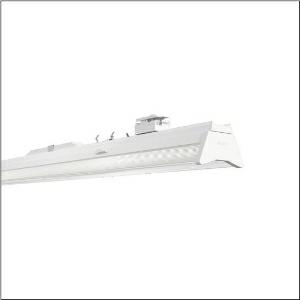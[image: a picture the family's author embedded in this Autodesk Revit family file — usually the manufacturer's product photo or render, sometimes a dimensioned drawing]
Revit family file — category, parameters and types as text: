
# Revit family: licross_r__21_performance_mo_51td16vn48xg_f21d
name_source: partatom
category: Lighting Fixtures
units: mm (PartAtom-declared; Revit-internal decimal feet)

## family parameters
Cut with Voids When Loaded = No
Host = Face
Light Source = No
Part Type = Normal
Room Calculation Point = No
Round Connector Dimension = Use Diameter
Shared = No

## types (1)
- --- (1 x LED, 8000 lm, 44.1 W, 4000K)
    Apparent Load = 44 VA
    CIE Flux Codes = 66 88 96 79 100
    Color Rendering = 80
    Color Temperature = 4000K
    Default Elevation = 1800 mm
    Description = Licross® 21 Performance MO, luminaire insert, of sheet steel, galvanised, coil coated, white, length: 1.500mm, width: 120mm, height: 123mm, LED rated luminous flux: 8.000lm, light colour: 840, control gear: DALI 2, CLO, with plug, 5-pole, with phase selection, mains connection: 220..240V, AC, 50/60Hz, start of lifetime: 44W, end of service life: 49W, internal wiring halogen-free, primary light control with lens, of plastic, primary optical cover: cover, of PMMA, light emission: direct/indirect distribution, primary light characteristic: symmetric, protection rating (complete): IP54, insulation class (complete): insulation class I (protective earthing), certification: CE, ENEC, VDE, UKCA, protection symbol: D if used in an environment with non-conductive dust loads with corresponding accessories, impact resistance: IK06, permissible ambient temperature for indoor applications: -25..+35°C, corresponds to IFS (International Featured Standards) requirements for safety and quality in the food industry, reducing of maximum allowable ambient temperature of 5°C with ceiling mounting, LABS conformity tested according to VDMA 24364:2018-05, packaging unit: 1 piece
    Height = 114 mm
    Lamp = 1 x LED
    Lamp Light Flux = 8000 lm
    Lamp Power = 44.1 W
    Lamp count = 1
    Length = 1500 mm
    Luminous efficacy = 181 lm/W
    Manufacturer = Siteco
    ModVariant = No
    Model = 51TD16VN48XG
    Mounting Place = Ceiling
    Mounting Type = Pendant
    Number of Poles = 1
    OnlyDefault = Yes
    Power Factor = 1
    Product Name = Licross® 21 Performance MO
    Product group = luminaire insert | ceiling pendant
    ProductGroupID = 902
    Protection Class = Protection class I
    Protection Degree = IP 54
    RLX_Detail_Level = 1
    RLX_Emergency_Light_Flux = 0 lm
    RLX_Emergency_Type = 0
    RLX_Emergency_Type_DB = No
    RlxData = <blob elided: 34165 chars, md5=22b59971>
    Socket = socket
    Standby Power = 0 W
    System Light Flux = 8000 lm
    System Power = 44 W
    Type Comments = factory setting: luminous flux: 100 % | dim-lin: 254 | 294 mA
    Type Image = l_1256138.jpg
    URL = http://relux.com
    VarID = @adj_109289
    Voltage = 0 V
    Weight = 0.00 kg
    Width = 120 mm

## geometry (parser evidence)
native form markers: Blend x4, Sweep x11
no freeform markers — native parametric forms only
